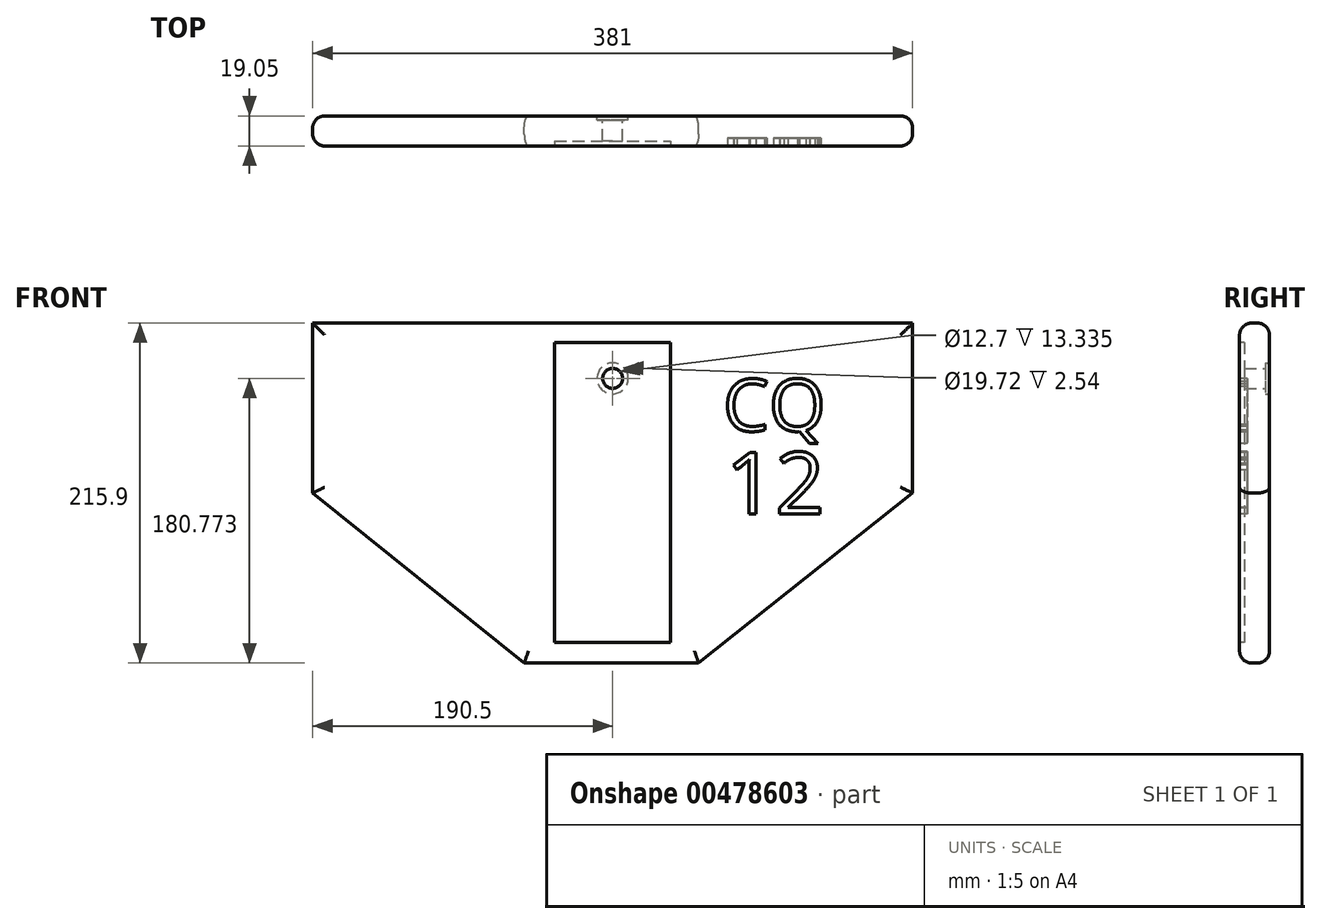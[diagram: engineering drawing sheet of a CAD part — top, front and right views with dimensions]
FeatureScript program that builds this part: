
annotation { "Feature Type Name" : "Feature", "Feature Type Description" : "" }
export const myFeature = defineFeature(function(context is Context, id is Id, definition is map)
    precondition{}
    {
        {
            var Q0;
            Q0=qCreatedBy(makeId("Front.planeOp"),FACE);
            var sketch = newSketch(context, id + "F0", { "sketchPlane" : qUnion([Q0])});
            skLineSegment(sketch, "E0.bottom", {"start": v(-190.5, 169.02) * mm, "end": v(190.5, 169.02) * mm});
            skLineSegment(sketch, "E0.top", {"start": v(-56.13, -46.88) * mm, "end": v(54.6, -46.88) * mm});
            skLineSegment(sketch, "E0.left", {"start": v(-190.5, 169.02) * mm, "end": v(-190.5, 61.07) * mm});
            skLineSegment(sketch, "E0.right", {"start": v(190.5, 169.02) * mm, "end": v(190.5, 61.07) * mm});
            skLineSegment(sketch, "E1", {"start": v(-190.5, 169.02) * mm, "end": v(-190.5, 140.45) * mm, "construction": true});
            skPoint(sketch, "E2", {"position": v(0, 169.02) * mm});
            skLineSegment(sketch, "E3", {"start": v(0, 169.02) * mm, "end": v(0, 0) * mm, "construction": true});
            skLineSegment(sketch, "E4", {"start": v(-190.5, 140.45) * mm, "end": v(0, 140.45) * mm, "construction": true});
            skCircle(sketch, "E5", {"center": v(0, 133.9) * mm, "radius": 6.35 * mm});
            skLineSegment(sketch, "E6", {"start": v(-190.5, 61.07) * mm, "end": v(-56.13, -46.88) * mm});
            skLineSegment(sketch, "E7", {"start": v(190.5, 61.07) * mm, "end": v(54.6, -46.88) * mm});
            skPoint(sketch, "E8.orphan", {"position": v(-190.5, -46.88) * mm});
            skPoint(sketch, "E9.orphan", {"position": v(190.5, -46.88) * mm});
            skSolve(sketch);
        }
        {
            var Q0;
            Q0=makeQuery(id+"F0.imprint","IMPRINT",FACE,{"disambiguationData":[TD([[makeQuery(id+"F0.imprint","IMPRINT",EDGE,{"derivedFrom":sQuery(id+"F0.wireOp",EDGE,"E0.bottom")}),-1.0]])]});
            extrude(context, id + "F1", {"entities" : qUnion([Q0]), "depth" : 19.05 * mm});
        }
        {
            var Q0;
            Q0=makeQuery(id+"F1.opExtrude","CAP_FACE",FACE,{"disambiguationData":[OSD([sQuery(id+"F0.wireOp",EDGE,"E0.bottom"),sQuery(id+"F0.wireOp",EDGE,"E0.top"),sQuery(id+"F0.wireOp",EDGE,"E0.left"),sQuery(id+"F0.wireOp",EDGE,"E0.right"),sQuery(id+"F0.wireOp",EDGE,"E5")])],"isStart":false});
            var sketch = newSketch(context, id + "F2", { "sketchPlane" : qUnion([Q0])});
            skLineSegment(sketch, "E10.bottom", {"start": v(-36.83, 156.8) * mm, "end": v(36.83, 156.8) * mm});
            skLineSegment(sketch, "E10.top", {"start": v(-36.83, -33.7) * mm, "end": v(36.83, -33.7) * mm});
            skLineSegment(sketch, "E10.left", {"start": v(-36.83, 156.8) * mm, "end": v(-36.83, -33.7) * mm});
            skLineSegment(sketch, "E10.right", {"start": v(36.83, 156.8) * mm, "end": v(36.83, -33.7) * mm});
            skPoint(sketch, "E11", {"position": v(0, 156.8) * mm});
            skPoint(sketch, "E12", {"position": v(0, 133.9) * mm});
            skLineSegment(sketch, "E13", {"start": v(0, 156.8) * mm, "end": v(0, 133.9) * mm, "construction": true});
            skSolve(sketch);
        }
        {
            var Q0;
            Q0=makeQuery(id+"F2.imprint","IMPRINT",FACE,{"disambiguationData":[TD([[makeQuery(id+"F2.imprint","IMPRINT",EDGE,{"derivedFrom":sQuery(id+"F2.wireOp",EDGE,"E10.bottom")}),-1.0]])]});
            var Q1;
            Q1=sQuery(id+"F2.wireOp",EDGE,"E10.left");
            var Q2;
            Q2=sQuery(id+"F2.wireOp",EDGE,"E10.bottom");
            var Q3;
            Q3=sQuery(id+"F2.wireOp",EDGE,"E10.right");
            var Q4;
            Q4=sQuery(id+"F2.wireOp",EDGE,"E10.top");
            extrude(context, id + "F3", {"entities" : qUnion([Q0]), "operationType" : NewBodyOperationType.REMOVE, "surfaceEntities" : qUnion([Q1, Q2, Q3, Q4]), "oppositeDirection" : true, "depth" : 3.17 * mm});
        }
        {
            var Q0;
            Q0=makeQuery(id+"F1.opExtrude","CAP_EDGE",EDGE,{"disambiguationData":[OSD([sQuery(id+"F0.wireOp",EDGE,"E0.bottom")])],"isStart":false});
            var Q1;
            Q1=makeQuery(id+"F1.opExtrude","CAP_EDGE",EDGE,{"disambiguationData":[OSD([sQuery(id+"F0.wireOp",EDGE,"E0.right")])],"isStart":false});
            var Q2;
            Q2=makeQuery(id+"F1.opExtrude","CAP_EDGE",EDGE,{"disambiguationData":[OSD([sQuery(id+"F0.wireOp",EDGE,"E0.top")])],"isStart":false});
            var Q3;
            Q3=makeQuery(id+"F1.opExtrude","CAP_EDGE",EDGE,{"disambiguationData":[OSD([sQuery(id+"F0.wireOp",EDGE,"E0.left")])],"isStart":false});
            var Q4;
            Q4=makeQuery(id+"F1.opExtrude","CAP_EDGE",EDGE,{"disambiguationData":[OSD([sQuery(id+"F0.wireOp",EDGE,"E0.bottom")])],"isStart":true});
            var Q5;
            Q5=makeQuery(id+"F1.opExtrude","CAP_EDGE",EDGE,{"disambiguationData":[OSD([sQuery(id+"F0.wireOp",EDGE,"E0.left")])],"isStart":true});
            var Q6;
            Q6=makeQuery(id+"F1.opExtrude","CAP_EDGE",EDGE,{"disambiguationData":[OSD([sQuery(id+"F0.wireOp",EDGE,"E0.top")])],"isStart":true});
            var Q7;
            Q7=makeQuery(id+"F1.opExtrude","CAP_EDGE",EDGE,{"disambiguationData":[OSD([sQuery(id+"F0.wireOp",EDGE,"E0.right")])],"isStart":true});
            var Q8;
            Q8=makeQuery(id+"F1.opExtrude","CAP_EDGE",EDGE,{"disambiguationData":[OSD([sQuery(id+"F0.wireOp",EDGE,"E6")])],"isStart":false});
            var Q9;
            Q9=makeQuery(id+"F1.opExtrude","CAP_EDGE",EDGE,{"disambiguationData":[OSD([sQuery(id+"F0.wireOp",EDGE,"E7")])],"isStart":false});
            var Q10;
            Q10=makeQuery(id+"F1.opExtrude","CAP_EDGE",EDGE,{"disambiguationData":[OSD([sQuery(id+"F0.wireOp",EDGE,"E6")])],"isStart":true});
            var Q11;
            Q11=makeQuery(id+"F1.opExtrude","CAP_EDGE",EDGE,{"disambiguationData":[OSD([sQuery(id+"F0.wireOp",EDGE,"E7")])],"isStart":true});
            fillet(context, id + "F4", {"entities" : qUnion([Q0, Q1, Q2, Q3, Q4, Q5, Q6, Q7, Q8, Q9, Q10, Q11]), "radius" : 7.62 * mm, "tangentPropagation" : true, "allowEdgeOverflow" : false});
        }
        {
            var Q0;
            Q0=makeQuery(id+"F1.opExtrude","CAP_FACE",FACE,{"disambiguationData":[OSD([sQuery(id+"F0.wireOp",EDGE,"E0.bottom"),sQuery(id+"F0.wireOp",EDGE,"E0.top"),sQuery(id+"F0.wireOp",EDGE,"E0.left"),sQuery(id+"F0.wireOp",EDGE,"E0.right"),sQuery(id+"F0.wireOp",EDGE,"E5"),sQuery(id+"F0.wireOp",EDGE,"E6"),sQuery(id+"F0.wireOp",EDGE,"E7")])],"isStart":false});
            var sketch = newSketch(context, id + "F5", { "sketchPlane" : qUnion([Q0])});
            skText(sketch, "E14", { "text": "12", "fontName": "OpenSans-Regular.ttf"});
            skText(sketch, "E15", { "text": "CQ", "fontName": "OpenSans-Regular.ttf"});
            const initialGuessF5  = {"E14": [0.0717, 0.04763, 1, 0, 0.03966], "E15": [0.07017, 0.1004, 1, 0, 0.03325]};
            skSetInitialGuess(sketch, initialGuessF5);
            skSolve(sketch);
        }
        {
            var Q0;
            Q0 = qSketchRegion(id + "F5", true);
            extrude(context, id + "F6", {"entities" : qUnion([Q0]), "operationType" : NewBodyOperationType.REMOVE, "oppositeDirection" : true, "depth" : 5.08 * mm});
        }
        {
            var Q0;
            Q0=makeQuery(id+"F1.opExtrude","CAP_FACE",FACE,{"disambiguationData":[OSD([sQuery(id+"F0.wireOp",EDGE,"E0.bottom"),sQuery(id+"F0.wireOp",EDGE,"E0.top"),sQuery(id+"F0.wireOp",EDGE,"E0.left"),sQuery(id+"F0.wireOp",EDGE,"E0.right"),sQuery(id+"F0.wireOp",EDGE,"E5"),sQuery(id+"F0.wireOp",EDGE,"E6"),sQuery(id+"F0.wireOp",EDGE,"E7")])],"isStart":true});
            var sketch = newSketch(context, id + "F7", { "sketchPlane" : qUnion([Q0])});
            skCircle(sketch, "E16", {"center": v(0, 133.9) * mm, "radius": 9.86 * mm});
            skSolve(sketch);
        }
        {
            var Q0;
            Q0 = qSketchRegion(id + "F7", true);
            extrude(context, id + "F8", {"entities" : qUnion([Q0]), "operationType" : NewBodyOperationType.REMOVE, "oppositeDirection" : true, "depth" : 2.54 * mm, "offsetDistance" : 25.4 * mm});
        }
    });
